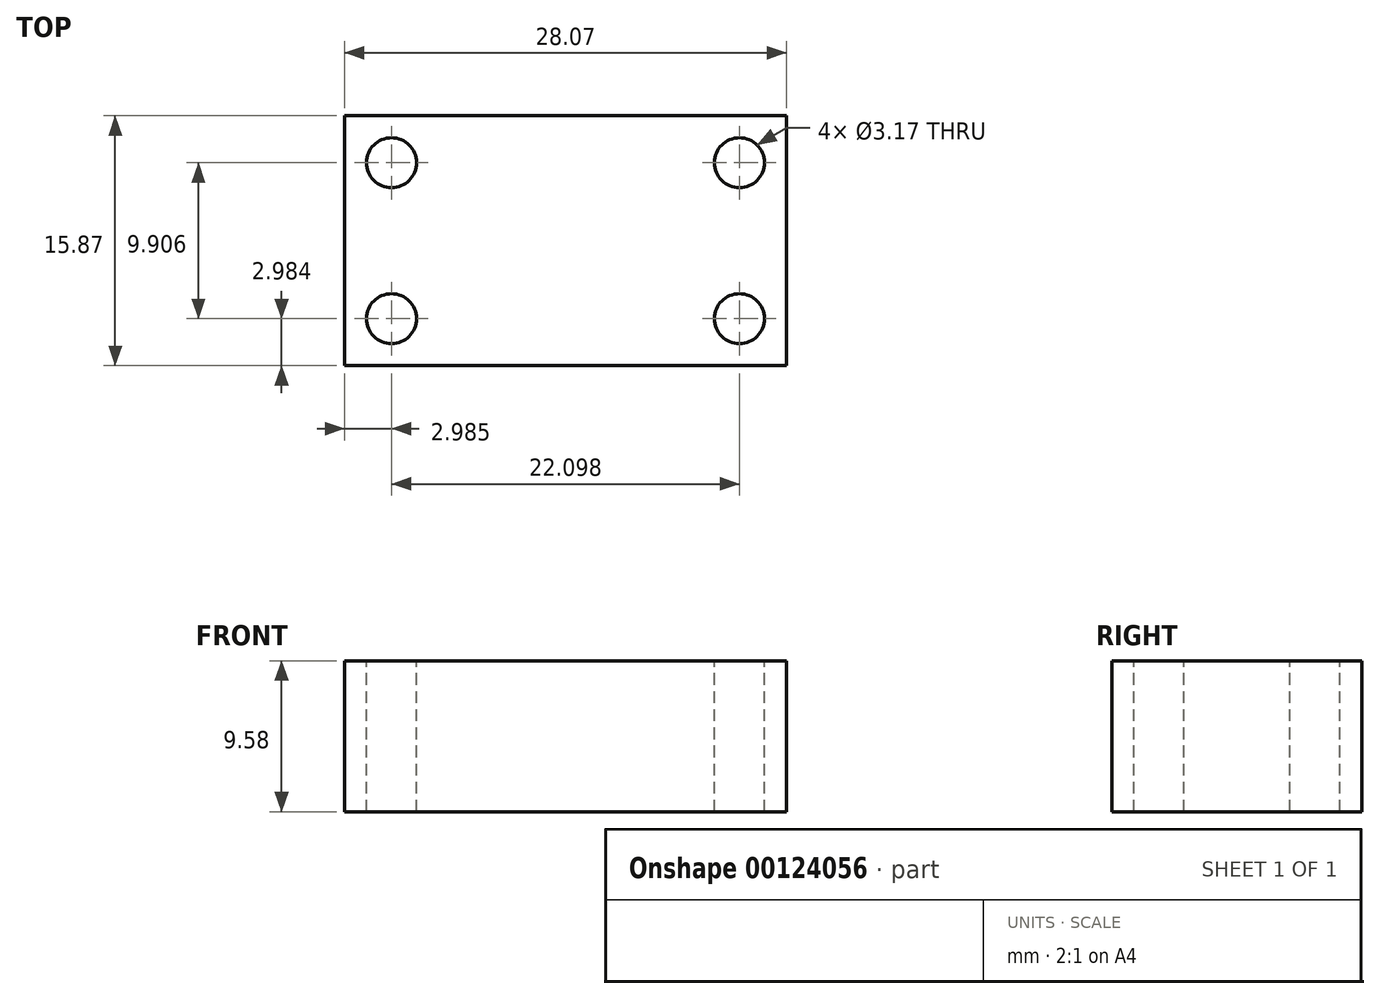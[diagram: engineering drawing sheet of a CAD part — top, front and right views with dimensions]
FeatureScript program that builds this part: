
annotation { "Feature Type Name" : "Feature", "Feature Type Description" : "" }
export const myFeature = defineFeature(function(context is Context, id is Id, definition is map)
    precondition{}
    {
        {
            var Q0;
            Q0=qCreatedBy(makeId("Top.planeOp"),FACE);
            var sketch = newSketch(context, id + "F0", { "sketchPlane" : qUnion([Q0])});
            skLineSegment(sketch, "E0.bottom", {"start": v(-43.46, 37.43) * mm, "end": v(-15.4, 37.43) * mm});
            skLineSegment(sketch, "E0.top", {"start": v(-43.46, 21.56) * mm, "end": v(-15.4, 21.56) * mm});
            skLineSegment(sketch, "E0.left", {"start": v(-43.46, 37.43) * mm, "end": v(-43.46, 21.56) * mm});
            skLineSegment(sketch, "E0.right", {"start": v(-15.4, 37.43) * mm, "end": v(-15.4, 21.56) * mm});
            skSolve(sketch);
        }
        {
            var Q0;
            Q0=makeQuery(id+"F0.imprint","IMPRINT",FACE,{"disambiguationData":[TD([[makeQuery(id+"F0.imprint","IMPRINT",EDGE,{"derivedFrom":sQuery(id+"F0.wireOp",EDGE,"E0.bottom")}),-1.0]])]});
            extrude(context, id + "F1", {"entities" : qUnion([Q0]), "depth" : 9.58 * mm});
        }
        {
            var Q0;
            Q0=makeQuery(id+"F1.opExtrude","CAP_FACE",FACE,{"disambiguationData":[OSD([sQuery(id+"F0.wireOp",EDGE,"E0.bottom"),sQuery(id+"F0.wireOp",EDGE,"E0.top"),sQuery(id+"F0.wireOp",EDGE,"E0.left"),sQuery(id+"F0.wireOp",EDGE,"E0.right")])],"isStart":false});
            var sketch = newSketch(context, id + "F2", { "sketchPlane" : qUnion([Q0])});
            skPoint(sketch, "E1", {"position": v(-18.38, 24.54) * mm});
            skPoint(sketch, "E2", {"position": v(-40.47, 24.54) * mm});
            skPoint(sketch, "E3", {"position": v(-40.47, 34.45) * mm});
            skPoint(sketch, "E4", {"position": v(-18.38, 34.45) * mm});
            skSolve(sketch);
        }
        {
            var Q0;
            Q0=sQuery(id+"F2.wireOp",VERTEX,"E3");
            var Q1;
            Q1=sQuery(id+"F2.wireOp",VERTEX,"E2");
            var Q2;
            Q2=sQuery(id+"F2.wireOp",VERTEX,"E1");
            var Q3;
            Q3=sQuery(id+"F2.wireOp",VERTEX,"E4");
            var Q4;
            Q4=makeQuery(id+"F1.opExtrude","SWEPT_BODY",BODY,{"disambiguationData":[OSD([sQuery(id+"F0.wireOp",EDGE,"E0.bottom"),sQuery(id+"F0.wireOp",EDGE,"E0.top"),sQuery(id+"F0.wireOp",EDGE,"E0.left"),sQuery(id+"F0.wireOp",EDGE,"E0.right")])]});
            hole(context, id + "F3", {"style" : HoleStyle.SIMPLE, "endStyle" : HoleEndStyle.THROUGH, "holeDiameter" : 3.17 * mm, "locations" : qUnion([Q0, Q1, Q2, Q3]), "scope" : qUnion([Q4]), "isTappedThrough" : true});
        }
    });
